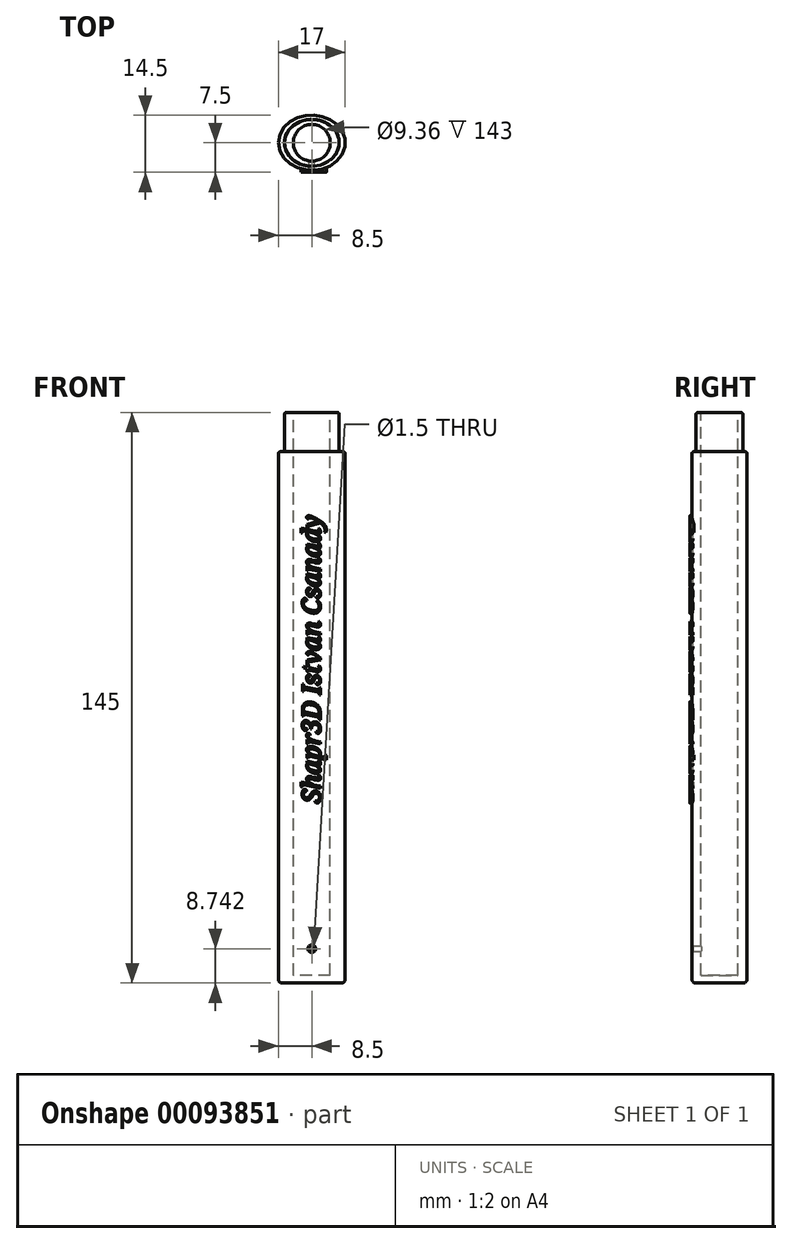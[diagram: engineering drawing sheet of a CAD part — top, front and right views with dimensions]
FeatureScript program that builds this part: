
annotation { "Feature Type Name" : "Feature", "Feature Type Description" : "" }
export const myFeature = defineFeature(function(context is Context, id is Id, definition is map)
    precondition{}
    {
        {
            var Q0;
            Q0=qCreatedBy(makeId("Top.planeOp"),FACE);
            var sketch = newSketch(context, id + "F0", { "sketchPlane" : qUnion([Q0])});
            skEllipse(sketch, "E0", {"center": v(0, 0) * mm, "majorRadius": 8.5 * mm, "minorRadius": 7 * mm, "majorAxis": v(-1, 0)});
            skCircle(sketch, "E1", {"center": v(0, 0) * mm, "radius": 4.55 * mm});
            skSolve(sketch);
        }
        {
            var Q0;
            Q0=qSketchRegion(id+"F0",true);
            var Q1;
            Q1=makeQuery(id+"F0.imprint","IMPRINT",FACE,{"disambiguationData":[TD([[makeQuery(id+"F0.imprint","IMPRINT",EDGE,{"derivedFrom":sQuery(id+"F0.wireOp",EDGE,"E1")}),1.0]])]});
            extrude(context, id + "F1", {"entities" : qUnion([Q0, Q1]), "depth" : 135 * mm});
        }
        {
            var Q0;
            Q0=makeQuery(id+"F1.opExtrude","CAP_FACE",FACE,{"disambiguationData":[OSD([sQuery(id+"F0.wireOp",EDGE,"E0")])],"isStart":false});
            var sketch = newSketch(context, id + "F2", { "sketchPlane" : qUnion([Q0])});
            skEllipse(sketch, "E2", {"center": v(0, 0) * mm, "majorRadius": 6.95 * mm, "minorRadius": 5.95 * mm, "majorAxis": v(-1, 0)});
            skSolve(sketch);
        }
        {
            var Q0;
            Q0=makeQuery(id+"F2.imprint","IMPRINT",FACE,{"disambiguationData":[TD([[makeQuery(id+"F2.imprint","IMPRINT",EDGE,{"derivedFrom":sQuery(id+"F2.wireOp",EDGE,"E2")}),1.0]])]});
            extrude(context, id + "F3", {"entities" : qUnion([Q0]), "operationType" : NewBodyOperationType.ADD, "depth" : 10 * mm});
        }
        {
            var Q0;
            Q0=makeQuery(id+"F3.opExtrude","CAP_FACE",FACE,{"disambiguationData":[OSD([sQuery(id+"F2.wireOp",EDGE,"E2")])],"isStart":false});
            var sketch = newSketch(context, id + "F4", { "sketchPlane" : qUnion([Q0])});
            skCircle(sketch, "E3", {"center": v(0, 0) * mm, "radius": 4.68 * mm});
            skSolve(sketch);
        }
        {
            var Q0;
            Q0=makeQuery(id+"F4.imprint","IMPRINT",FACE,{"disambiguationData":[TD([[makeQuery(id+"F4.imprint","IMPRINT",EDGE,{"derivedFrom":sQuery(id+"F4.wireOp",EDGE,"E3")}),1.0]])]});
            extrude(context, id + "F5", {"entities" : qUnion([Q0]), "operationType" : NewBodyOperationType.REMOVE, "oppositeDirection" : true, "depth" : 143 * mm});
        }
        {
            var Q0;
            Q0=makeQuery(id+"F5.boolean.opBoolean","COPY",EDGE,{"derivedFrom":makeQuery(id+"F5.opExtrude","CAP_EDGE",EDGE,{"disambiguationData":[OSD([sQuery(id+"F4.wireOp",EDGE,"E3")])],"isStart":true})});
            var Q1;
            Q1=makeQuery(id+"F3.opExtrude","CAP_EDGE",EDGE,{"disambiguationData":[OSD([sQuery(id+"F2.wireOp",EDGE,"E2")])],"isStart":false});
            var Q2;
            Q2=makeQuery(id+"F1.opExtrude","CAP_EDGE",EDGE,{"disambiguationData":[OSD([sQuery(id+"F0.wireOp",EDGE,"E0")])],"isStart":false});
            fillet(context, id + "F6", {"entities" : qUnion([Q0, Q1, Q2]), "radius" : .5 * mm, "tangentPropagation" : true, "allowEdgeOverflow" : false});
        }
        {
            var Q0;
            Q0=makeQuery(id+"F1.opExtrude","CAP_EDGE",EDGE,{"disambiguationData":[OSD([sQuery(id+"F0.wireOp",EDGE,"E0")])],"isStart":true});
            fillet(context, id + "F7", {"entities" : qUnion([Q0]), "radius" : 1 * mm, "tangentPropagation" : true, "allowEdgeOverflow" : false});
        }
        {
            var Q0;
            Q0=qCreatedBy(makeId("Front.planeOp"),FACE);
            var sketch = newSketch(context, id + "F8", { "sketchPlane" : qUnion([Q0])});
            skCircle(sketch, "E4", {"center": v(0, 8.74) * mm, "radius": 0.75 * mm});
            skSolve(sketch);
        }
        {
            var Q0;
            Q0=qSketchRegion(id+"F8",true);
            extrude(context, id + "F9", {"entities" : qUnion([Q0]), "operationType" : NewBodyOperationType.REMOVE, "depth" : 25 * mm});
        }
        {
            var Q0;
            Q0=makeQuery(id+"F9.boolean.opBoolean","INTERSECT",EDGE,{"derivedFrom":[makeQuery(id+"F1.opExtrude","SWEPT_FACE",FACE,{"disambiguationData":[OSD([sQuery(id+"F0.wireOp",EDGE,"E0")])]}),makeQuery(id+"F9.opExtrude","SWEPT_FACE",FACE,{"disambiguationData":[OSD([sQuery(id+"F8.wireOp",EDGE,"E4")])]})]});
            fillet(context, id + "F10", {"entities" : qUnion([Q0]), "radius" : .2 * mm, "tangentPropagation" : true, "allowEdgeOverflow" : false});
        }
        {
            var Q0;
            Q0=qCreatedBy(makeId("Front.planeOp"),FACE);
            cPlane(context, id + "F11", {"entities" : qUnion([Q0]), "cplaneType" : CPlaneType.OFFSET, "offset" : 7.5 * mm, "width" : 150 * mm, "height" : 150 * mm});
        }
        {
            var Q0;
            Q0=qCreatedBy(id+"F11.planeOp",FACE);
            var sketch = newSketch(context, id + "F12", { "sketchPlane" : qUnion([Q0])});
            skText(sketch, "E5", { "text": "Shapr3D Istvan Csanady", "fontName": "NotoSerif-Italic.ttf"});
            const initialGuessF12  = {"E5": [0.00218, 0.04569, 0, 1, 0.00461]};
            skSetInitialGuess(sketch, initialGuessF12);
            skSolve(sketch);
        }
        {
            var Q0;
            Q0=qSketchRegion(id+"F12",true);
            extrude(context, id + "F13", {"entities" : qUnion([Q0]), "operationType" : NewBodyOperationType.ADD, "oppositeDirection" : true, "depth" : 1 * mm});
        }
    });
